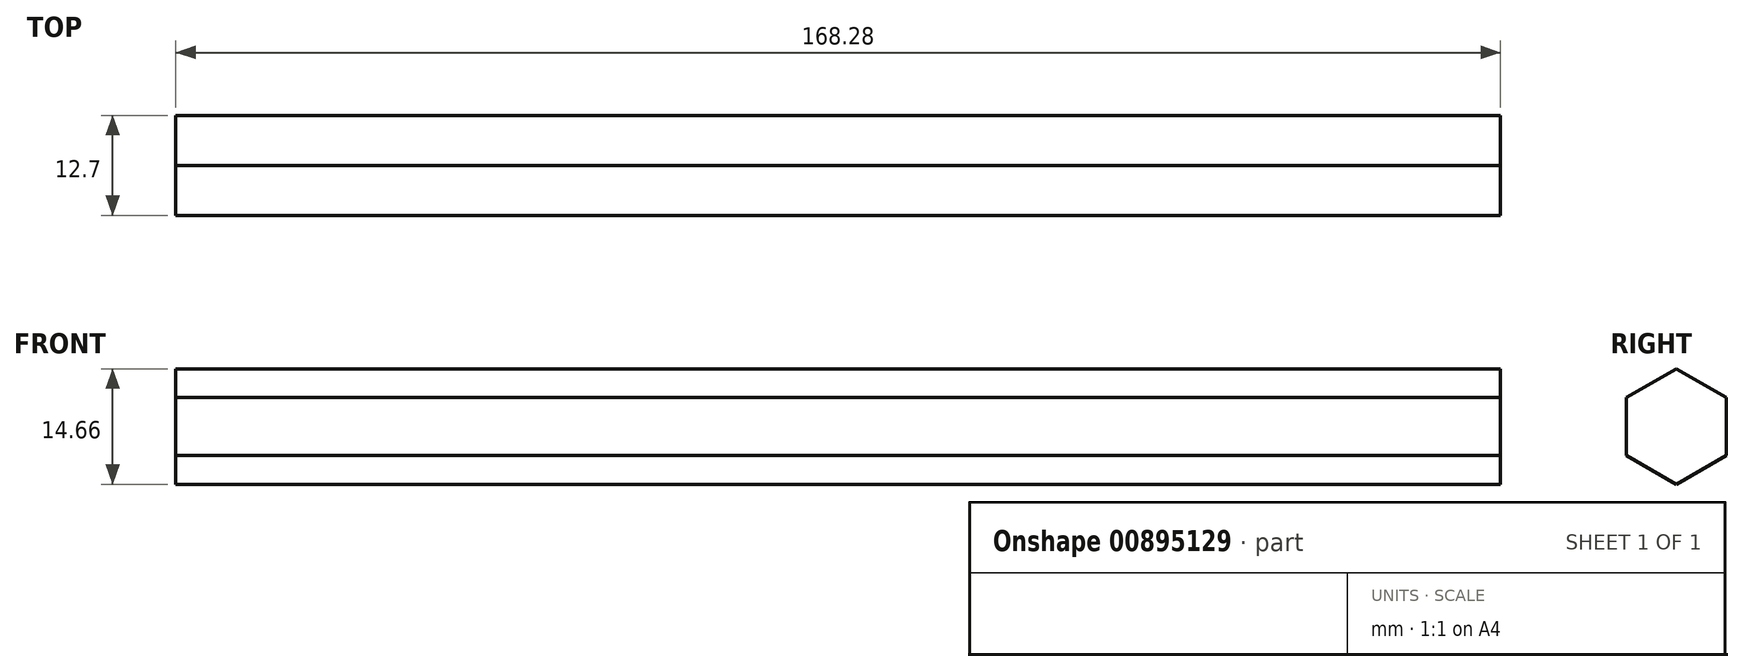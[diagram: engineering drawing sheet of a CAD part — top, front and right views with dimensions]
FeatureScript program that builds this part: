
annotation { "Feature Type Name" : "Feature", "Feature Type Description" : "" }
export const myFeature = defineFeature(function(context is Context, id is Id, definition is map)
    precondition{}
    {
        {
            var Q0;
            Q0=qCreatedBy(makeId("Right.planeOp"),FACE);
            var sketch = newSketch(context, id + "F0", { "sketchPlane" : qUnion([Q0])});
            skCircle(sketch, "E0.cCircle", {"center": v(0, 0) * mm, "radius": 6.35 * mm, "construction": true});
            skLineSegment(sketch, "E0.0", {"start": v(0, 7.33) * mm, "end": v(6.35, 3.67) * mm});
            skLineSegment(sketch, "E0.1", {"start": v(6.35, 3.67) * mm, "end": v(6.35, -3.67) * mm});
            skLineSegment(sketch, "E0.2", {"start": v(6.35, -3.67) * mm, "end": v(0, -7.33) * mm});
            skLineSegment(sketch, "E0.3", {"start": v(0, -7.33) * mm, "end": v(-6.35, -3.67) * mm});
            skLineSegment(sketch, "E0.4", {"start": v(-6.35, -3.67) * mm, "end": v(-6.35, 3.67) * mm});
            skLineSegment(sketch, "E0.5", {"start": v(-6.35, 3.67) * mm, "end": v(0, 7.33) * mm});
            skPoint(sketch, "E0.0.midPoint", {"position": v(3.17, 5.5) * mm});
            skSolve(sketch);
        }
        {
            var Q0;
            Q0 = qSketchRegion(id + "F0", true);
            extrude(context, id + "F1", {"entities" : qUnion([Q0]), "depth" : 168.27 * mm, "offsetDistance" : 25.4 * mm});
        }
    });
